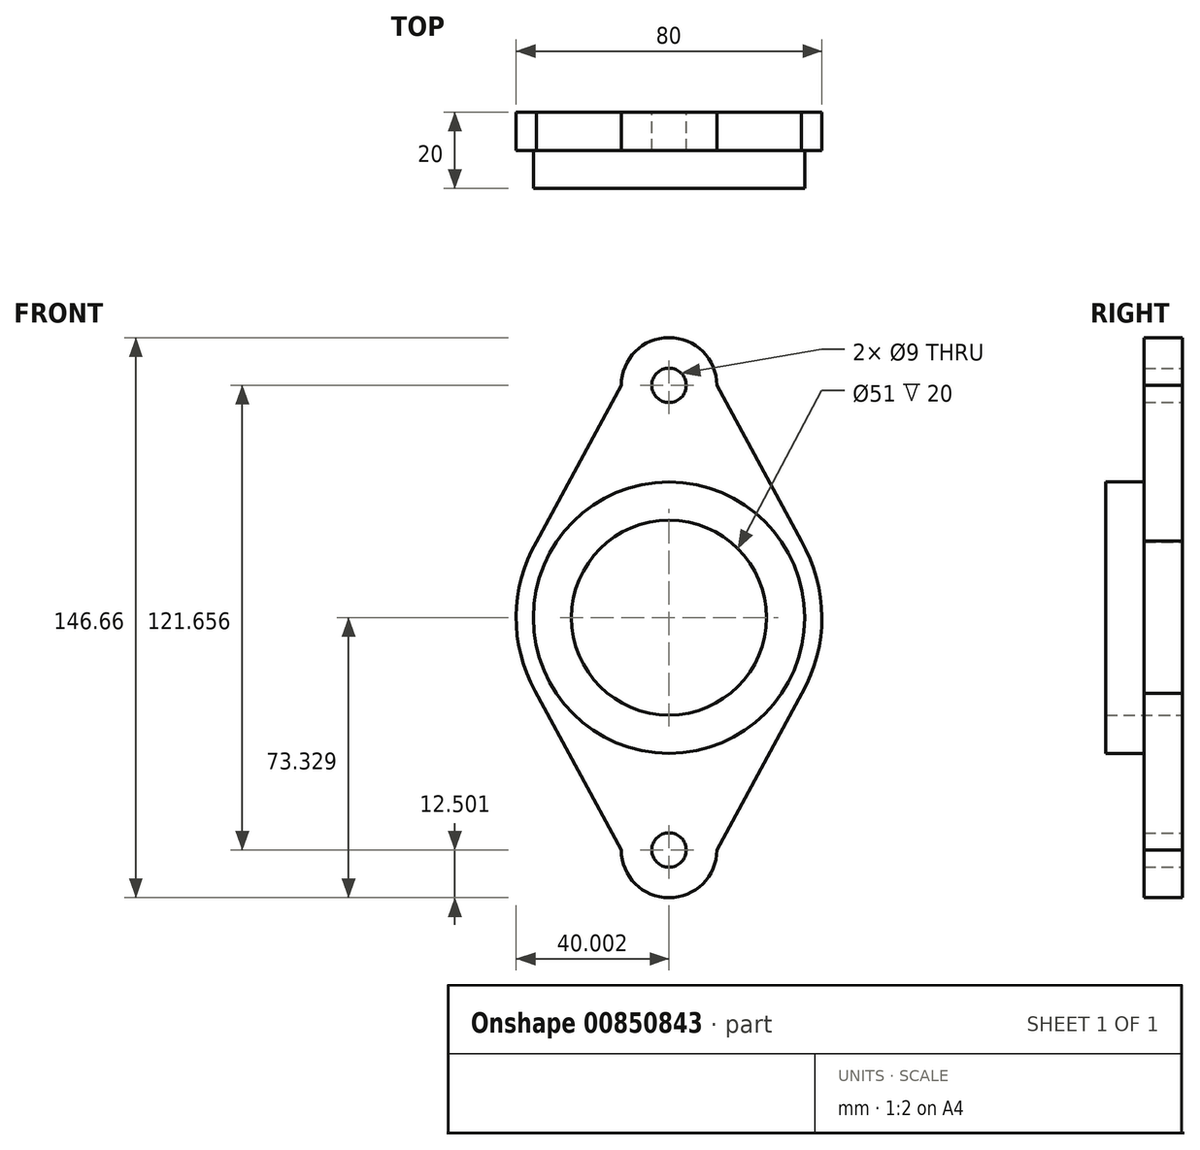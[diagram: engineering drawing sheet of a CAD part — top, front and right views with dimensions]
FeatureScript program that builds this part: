
annotation { "Feature Type Name" : "Feature", "Feature Type Description" : "" }
export const myFeature = defineFeature(function(context is Context, id is Id, definition is map)
    precondition{}
    {
        {
            var Q0;
            Q0=qCreatedBy(makeId("Front.planeOp"),FACE);
            var sketch = newSketch(context, id + "F0", { "sketchPlane" : qUnion([Q0])});
            skCircle(sketch, "E0", {"center": v(-78.97, 5.16) * mm, "radius": 25.5 * mm});
            skCircle(sketch, "E1", {"center": v(-78.97, 5.16) * mm, "radius": 35.5 * mm});
            skCircle(sketch, "E2", {"center": v(-78.97, 65.99) * mm, "radius": 4.5 * mm});
            skCircle(sketch, "E3", {"center": v(-78.97, -55.67) * mm, "radius": 4.5 * mm});
            skLineSegment(sketch, "E4", {"start": v(-78.97, 5.16) * mm, "end": v(-118.97, 5.16) * mm});
            skLineSegment(sketch, "E5", {"start": v(-78.97, 5.16) * mm, "end": v(-38.97, 5.16) * mm});
            skArc(sketch, "E6", {"start": v(-118.97, 5.16) * mm, "mid": v(-117.63, 15.41) * mm, "end": v(-113.71, 24.98) * mm});
            skArc(sketch, "E7", {"start": v(-118.97, 5.16) * mm, "mid": v(-117.72, -4.74) * mm, "end": v(-114.07, -14.02) * mm});
            skArc(sketch, "E8", {"start": v(-38.97, 5.16) * mm, "mid": v(-40.34, 15.56) * mm, "end": v(-44.37, 25.24) * mm});
            skArc(sketch, "E9", {"start": v(-38.97, 5.16) * mm, "mid": v(-40.3, -5.07) * mm, "end": v(-44.2, -14.61) * mm});
            skArc(sketch, "E10", {"start": v(-91.47, 65.99) * mm, "mid": v(-78.97, 78.49) * mm, "end": v(-66.47, 65.99) * mm});
            skArc(sketch, "E11", {"start": v(-91.47, -55.67) * mm, "mid": v(-78.97, -68.17) * mm, "end": v(-66.47, -55.67) * mm});
            skLineSegment(sketch, "E12", {"start": v(-91.47, 65.99) * mm, "end": v(-113.71, 24.98) * mm});
            skLineSegment(sketch, "E13", {"start": v(-66.47, 65.99) * mm, "end": v(-44.37, 25.24) * mm});
            skLineSegment(sketch, "E14", {"start": v(-114.07, -14.02) * mm, "end": v(-91.47, -55.67) * mm});
            skLineSegment(sketch, "E15", {"start": v(-44.2, -14.61) * mm, "end": v(-66.47, -55.67) * mm});
            skSolve(sketch);
        }
        {
            var Q0;
            Q0=makeQuery(id+"F0.imprint","IMPRINT",FACE,{"disambiguationData":[TD([[makeQuery(id+"F0.imprint","IMPRINT",EDGE,{"derivedFrom":sQuery(id+"F0.wireOp",EDGE,"E2")}),-1.0]])]});
            var Q1;
            Q1=makeQuery(id+"F0.imprint","IMPRINT",FACE,{"disambiguationData":[TD([[makeQuery(id+"F0.imprint","IMPRINT",EDGE,{"derivedFrom":sQuery(id+"F0.wireOp",EDGE,"E3")}),-1.0]])]});
            extrude(context, id + "F1", {"entities" : qUnion([Q0, Q1]), "depth" : 10 * mm, "offsetDistance" : 25.4 * mm});
        }
        {
            var Q0;
            {var subQ0=sQuery(id+"F0.wireOp",EDGE,"E4");var subQ1=sQuery(id+"F0.wireOp",EDGE,"E0");var subQ2=makeQuery(id+"F0.imprint","INTERSECT",VERTEX,{"derivedFrom":[subQ1,subQ0]});Q0=makeQuery(id+"F0.imprint","IMPRINT",FACE,{"disambiguationData":[TD([[makeQuery(id+"F0.imprint","IMPRINT",EDGE,{"disambiguationData":[TD([[subQ2,-1.0]])],"derivedFrom":subQ1}),-1.0]])]});}
            var Q1;
            {var subQ0=sQuery(id+"F0.wireOp",EDGE,"E4");var subQ1=sQuery(id+"F0.wireOp",EDGE,"E0");var subQ2=makeQuery(id+"F0.imprint","INTERSECT",VERTEX,{"derivedFrom":[subQ1,subQ0]});Q1=makeQuery(id+"F0.imprint","IMPRINT",FACE,{"disambiguationData":[TD([[makeQuery(id+"F0.imprint","IMPRINT",EDGE,{"disambiguationData":[TD([[subQ2,1.0]])],"derivedFrom":subQ1}),-1.0]])]});}
            extrude(context, id + "F2", {"entities" : qUnion([Q0, Q1]), "operationType" : NewBodyOperationType.ADD, "depth" : 20 * mm, "offsetDistance" : 25.4 * mm});
        }
    });
